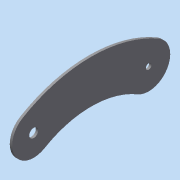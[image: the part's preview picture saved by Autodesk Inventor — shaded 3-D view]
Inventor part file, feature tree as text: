
AUTODESK INVENTOR PART (.ipt)
format: ipt  version: 2015 (Build 190159000, 159)  size: 92,160 bytes
history: native  units: in
note: dims shown in document units (in); Inventor stores cm internally (conversion verified against a paired STEP export)
features: extrude x2, sketch x2
ambient origin geometry x8: Origin, YZ Plane, XZ Plane, XY Plane, X Axis, Y Axis, Z Axis, Center Point
bodies: Solid1 (feature_tree)
feature tree (4):
  extrude  "Extrusion1"  Depth=4.0in
  extrude  "Extrusion3"  Depth=0.083in
  sketch  "Sketch1"  dims[d9=4.0in d10=1.5in]
  sketch  "Sketch3"  dims[d11=0.083in d12=0.0in d13=0.3125in d14=0.3125in d19=0.3125in d20=0.1969in d21=0.1969in d22=0.0in]
